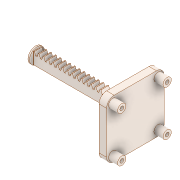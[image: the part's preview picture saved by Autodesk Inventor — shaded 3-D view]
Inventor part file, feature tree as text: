
AUTODESK INVENTOR PART (.ipt)
format: ipt  version: 2020 (Build 240168000, 168)  size: 271,872 bytes
history: mixed  units: mm
features: extrude x4, sketch x4, fillet x1, other x1, imported_body x1
ambient origin geometry x8: Origin, YZ Plane, XZ Plane, XY Plane, X Axis, Y Axis, Z Axis, Center Point
bodies: Solid1 (imported_parasolid)
feature tree (11):
  extrude  "Extrusion1"  Depth=38.0mm
  extrude  "Extrusion2"  Depth=5.0mm TaperAngle=0.0deg
  extrude  "Extrusion3"  Depth=2.5mm
  extrude  "Extrusion4"  Depth=5.0mm
  fillet  "Fillet1"  Radius=4.0mm
  sketch  "Sketch1"  dims[d0=5.0mm d1=0.0mm d2=38.0mm]
  sketch  "Sketch2"  dims[d3=38.0mm d4=5.0mm d5=0.0mm]
  sketch  "Sketch3"  dims[d6=2.5mm d7=2.5mm]
  sketch  "Sketch4"  dims[d8=2.5mm d9=2.5mm d10=4.0mm d11=4.0mm d12=5.0mm d13=0.0mm d14=5.5mm d15=5.5mm d16=5.5mm d17=5.5mm d18=6.0mm d19=0.0mm d20=5.0mm]
  other  "Boss-Extrude6"
  imported_body  NMx_Import_Brep_tag  [imported B-rep: ~151 faces, bbox_mm=[72.0, 38.0, 38.0]]
